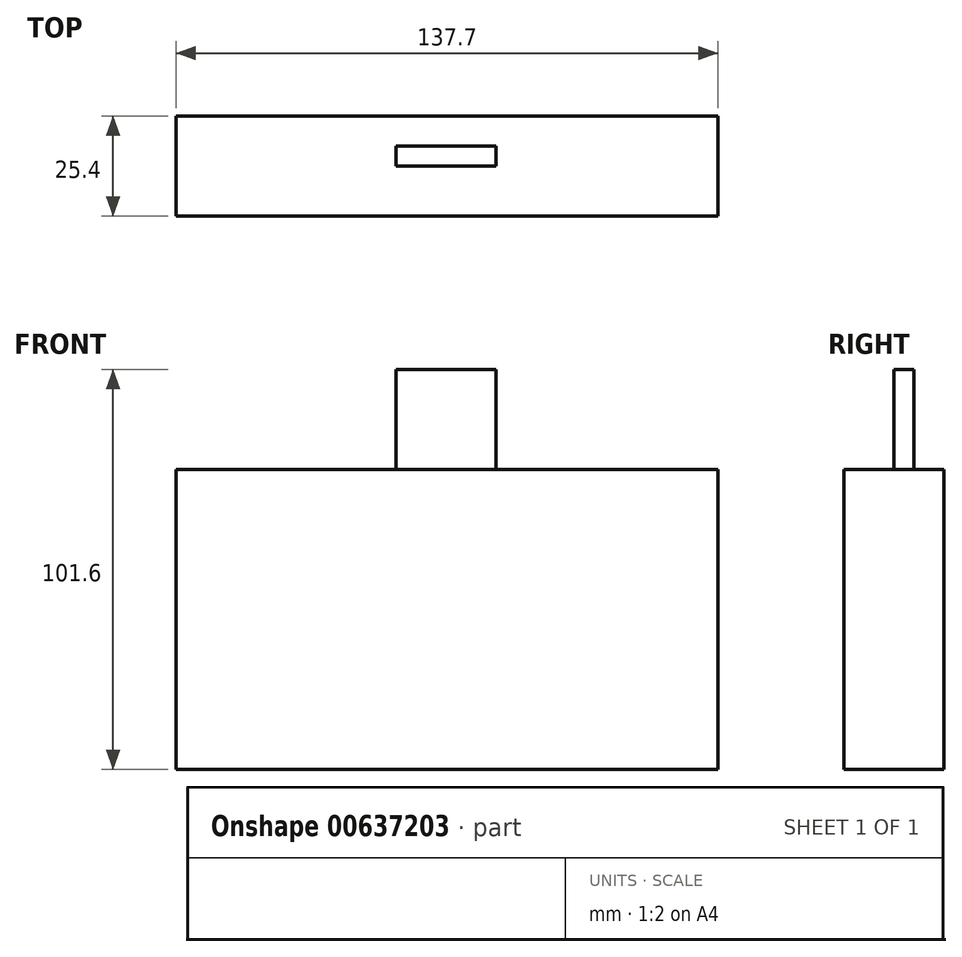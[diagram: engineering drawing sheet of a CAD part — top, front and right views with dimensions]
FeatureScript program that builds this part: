
annotation { "Feature Type Name" : "Feature", "Feature Type Description" : "" }
export const myFeature = defineFeature(function(context is Context, id is Id, definition is map)
    precondition{}
    {
        {
            var Q0;
            Q0=qCreatedBy(makeId("Front.planeOp"),FACE);
            var sketch = newSketch(context, id + "F0", { "sketchPlane" : qUnion([Q0])});
            skLineSegment(sketch, "E0", {"start": v(-35.4, 55.28) * mm, "end": v(-35.4, -20.92) * mm});
            skLineSegment(sketch, "E1", {"start": v(-35.4, -20.92) * mm, "end": v(102.3, -20.92) * mm});
            skLineSegment(sketch, "E2", {"start": v(102.3, -20.92) * mm, "end": v(102.3, 55.28) * mm});
            skLineSegment(sketch, "E3", {"start": v(102.3, 55.28) * mm, "end": v(-35.4, 55.28) * mm});
            skSolve(sketch);
        }
        {
            var Q0;
            Q0 = qSketchRegion(id + "F0", true);
            var Q1;
            Q1 = qConstructionFilter(qBodyType(qCreatedBy(id + "F0" ,EDGE), BodyType.WIRE), ConstructionObject.NO);
            extrude(context, id + "F1", {"entities" : qUnion([Q0]), "surfaceOperationType" : NewSurfaceOperationType.ADD, "surfaceEntities" : qUnion([Q1]), "depth" : 10.92 * mm, "offsetDistance" : 25.4 * mm});
        }
        {
            var Q0;
            Q0 = qSketchRegion(id + "F0", true);
            extrude(context, id + "F2", {"entities" : qUnion([Q0]), "operationType" : NewBodyOperationType.ADD, "depth" : 25.4 * mm, "offsetDistance" : 25.4 * mm});
        }
        {
            var Q0;
            {var subQ0=sQuery(id+"F0.wireOp",EDGE,"E3");Q0=makeQuery(id+"F2.boolean.opBoolean","MERGE",FACE,{"derivedFrom":[makeQuery(id+"F1.opExtrude","SWEPT_FACE",FACE,{"disambiguationData":[OSD([subQ0])]}),makeQuery(id+"F2.opExtrude","SWEPT_FACE",FACE,{"disambiguationData":[OSD([subQ0])]})]});}
            var sketch = newSketch(context, id + "F3", { "sketchPlane" : qUnion([Q0])});
            skLineSegment(sketch, "E4", {"start": v(20.41, -7.62) * mm, "end": v(20.41, -12.7) * mm});
            skPoint(sketch, "E4.endSnap0", {"position": v(-35.4, -12.7) * mm});
            skLineSegment(sketch, "E5", {"start": v(20.41, -12.7) * mm, "end": v(45.81, -12.7) * mm});
            skLineSegment(sketch, "E6", {"start": v(45.81, -12.7) * mm, "end": v(45.81, -7.62) * mm});
            skLineSegment(sketch, "E7", {"start": v(45.81, -7.62) * mm, "end": v(20.41, -7.62) * mm});
            skSolve(sketch);
        }
        {
            var Q0;
            Q0 = qSketchRegion(id + "F3", true);
            extrude(context, id + "F4", {"entities" : qUnion([Q0]), "operationType" : NewBodyOperationType.ADD, "depth" : 25.4 * mm, "offsetDistance" : 25.4 * mm});
        }
    });
